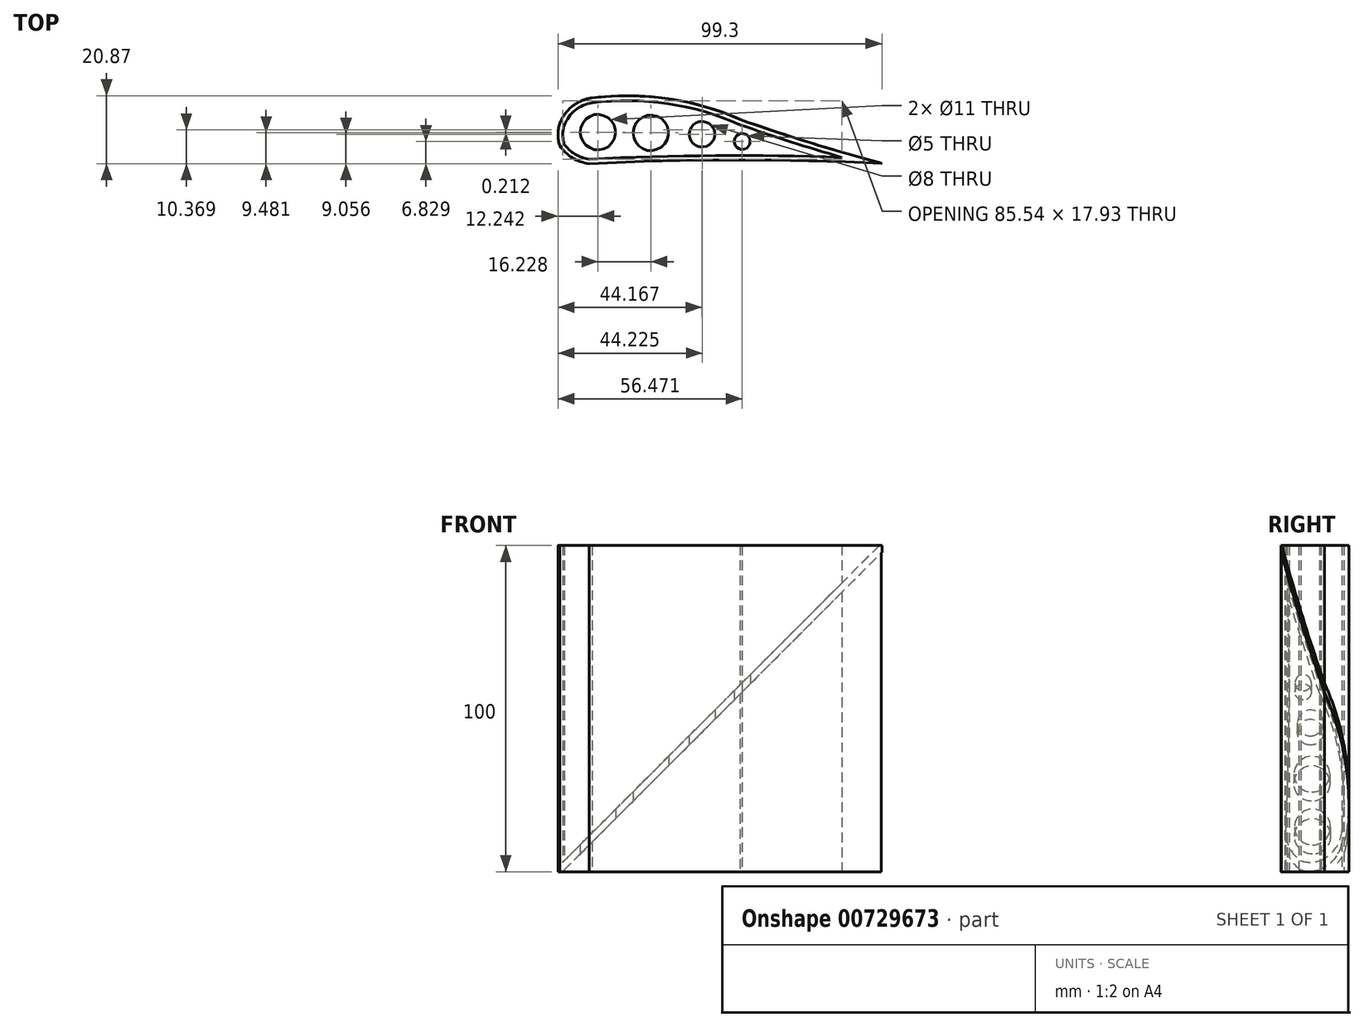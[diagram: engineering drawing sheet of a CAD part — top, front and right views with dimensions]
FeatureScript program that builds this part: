
annotation { "Feature Type Name" : "Feature", "Feature Type Description" : "" }
export const myFeature = defineFeature(function(context is Context, id is Id, definition is map)
    precondition{}
    {
        {
            var Q0;
            Q0=qCreatedBy(makeId("Top.planeOp"),FACE);
            var sketch = newSketch(context, id + "F0", { "sketchPlane" : qUnion([Q0])});
            skArc(sketch, "E0", {"start": v(-50.4, 5.52) * mm, "mid": v(-46.5, 1.8) * mm, "end": v(-41.43, 0) * mm});
            skArc(sketch, "E1", {"start": v(-50.4, 12.4) * mm, "mid": v(-50.96, 8.96) * mm, "end": v(-50.4, 5.52) * mm});
            skArc(sketch, "E2", {"start": v(-40.6, 20.25) * mm, "mid": v(-46.58, 17.68) * mm, "end": v(-50.4, 12.4) * mm});
            skArc(sketch, "E3", {"start": v(5.5, 13.44) * mm, "mid": v(-17.09, 20.01) * mm, "end": v(-40.6, 20.25) * mm});
            skArc(sketch, "E4", {"start": v(5.5, 13.44) * mm, "mid": v(27.14, 6.3) * mm, "end": v(49.04, 0) * mm});
            skArc(sketch, "E5", {"start": v(49.04, 0) * mm, "mid": v(3.8, 1.13) * mm, "end": v(-41.43, 0) * mm});
            skLineSegment(sketch, "E6", {"start": v(-50.96, 18.95) * mm, "end": v(-50.96, 0) * mm});
            skLineSegment(sketch, "E7", {"start": v(49.04, 0) * mm, "end": v(49.04, 12.24) * mm});
            skArc(sketch, "E8.0", {"start": v(4.93, 12.05) * mm, "mid": v(-17.27, 18.52) * mm, "end": v(-40.4, 18.76) * mm});
            skArc(sketch, "E8.1", {"start": v(-48.98, 11.9) * mm, "mid": v(-49.45, 9.05) * mm, "end": v(-49.04, 6.2) * mm});
            skArc(sketch, "E8.2", {"start": v(-49.04, 6.2) * mm, "mid": v(-45.68, 3.06) * mm, "end": v(-41.36, 1.5) * mm});
            skArc(sketch, "E8.3", {"start": v(-40.4, 18.76) * mm, "mid": v(-45.63, 16.51) * mm, "end": v(-48.98, 11.9) * mm});
            skArc(sketch, "E8.4", {"start": v(36.09, 2.06) * mm, "mid": v(-2.65, 2.6) * mm, "end": v(-41.36, 1.5) * mm});
            skArc(sketch, "E8.5", {"start": v(4.93, 12.05) * mm, "mid": v(20.44, 6.84) * mm, "end": v(36.09, 2.06) * mm});
            skSolve(sketch);
        }
        {
            var Q0;
            Q0=qCreatedBy(makeId("Front.planeOp"),FACE);
            var sketch = newSketch(context, id + "F1", { "sketchPlane" : qUnion([Q0])});
            skLineSegment(sketch, "E9", {"start": v(-50.95, 0) * mm, "end": v(-50.95, 1.41) * mm});
            skLineSegment(sketch, "E10", {"start": v(-50.95, 0) * mm, "end": v(-49.53, 0) * mm});
            skLineSegment(sketch, "E11.MirrorCS", {"start": v(49.05, 100) * mm, "end": v(47.64, 100) * mm});
            skLineSegment(sketch, "E12.MirrorCS", {"start": v(49.05, 100) * mm, "end": v(49.05, 98.59) * mm});
            skLineSegment(sketch, "E13", {"start": v(-50.95, 1.41) * mm, "end": v(47.64, 100) * mm});
            skLineSegment(sketch, "E14", {"start": v(49.05, 98.59) * mm, "end": v(-49.53, 0) * mm});
            skSolve(sketch);
        }
        {
            var Q0;
            Q0=qCreatedBy(makeId("Top.planeOp"),FACE);
            var sketch = newSketch(context, id + "F2", { "sketchPlane" : qUnion([Q0])});
            skArc(sketch, "E15", {"start": v(-50.35, 5.62) * mm, "mid": v(-46.46, 1.91) * mm, "end": v(-41.4, 0.1) * mm});
            skArc(sketch, "E16", {"start": v(-50.35, 12.44) * mm, "mid": v(-50.9, 9.03) * mm, "end": v(-50.35, 5.62) * mm});
            skArc(sketch, "E17", {"start": v(-40.56, 20.28) * mm, "mid": v(-46.54, 17.71) * mm, "end": v(-50.35, 12.44) * mm});
            skArc(sketch, "E18", {"start": v(5.48, 13.48) * mm, "mid": v(-17.07, 20.05) * mm, "end": v(-40.56, 20.28) * mm});
            skArc(sketch, "E19", {"start": v(5.48, 13.48) * mm, "mid": v(26.81, 6.44) * mm, "end": v(48.4, 0.21) * mm});
            skArc(sketch, "E20", {"start": v(48.4, 0.21) * mm, "mid": v(3.5, 1.27) * mm, "end": v(-41.4, 0.1) * mm});
            skLineSegment(sketch, "E21.bottom", {"start": v(-65.42, 35.82) * mm, "end": v(65.5, 35.82) * mm});
            skLineSegment(sketch, "E21.top", {"start": v(-65.42, -21.35) * mm, "end": v(65.5, -21.35) * mm});
            skLineSegment(sketch, "E21.left", {"start": v(-65.42, 35.82) * mm, "end": v(-65.42, -21.35) * mm});
            skLineSegment(sketch, "E21.right", {"start": v(65.5, 35.82) * mm, "end": v(65.5, -21.35) * mm});
            skSolve(sketch);
        }
        {
            var Q0;
            {var subQ0=sQuery(id+"F0.wireOp",EDGE,"E0");Q0=makeQuery(id+"F0.imprint","IMPRINT",FACE,{"disambiguationData":[TD([[makeQuery(id+"F0.imprint","IMPRINT",EDGE,{"derivedFrom":subQ0}),1.0]])]});}
            extrude(context, id + "F3", {"entities" : qUnion([Q0]), "depth" : 100 * mm, "offsetDistance" : 25 * mm});
        }
        {
            var Q0;
            Q0=makeQuery(id+"F1.imprint","IMPRINT",FACE,{"disambiguationData":[TD([[makeQuery(id+"F1.imprint","IMPRINT",EDGE,{"derivedFrom":sQuery(id+"F1.wireOp",EDGE,"E9")}),-1.0]])]});
            extrude(context, id + "F4", {"entities" : qUnion([Q0]), "operationType" : NewBodyOperationType.ADD, "oppositeDirection" : true, "depth" : 25 * mm, "offsetDistance" : 25 * mm});
        }
        {
            var Q0;
            Q0=makeQuery(id+"F2.imprint","IMPRINT",FACE,{"disambiguationData":[TD([[makeQuery(id+"F2.imprint","IMPRINT",EDGE,{"derivedFrom":sQuery(id+"F2.wireOp",EDGE,"E15")}),-1.0]])]});
            var Q1;
            Q1=makeQuery(id+"F3.opExtrude","CAP_FACE",FACE,{"disambiguationData":[OSD([sQuery(id+"F0.wireOp",EDGE,"E0"),sQuery(id+"F0.wireOp",EDGE,"E1"),sQuery(id+"F0.wireOp",EDGE,"E2"),sQuery(id+"F0.wireOp",EDGE,"E3"),sQuery(id+"F0.wireOp",EDGE,"E4"),sQuery(id+"F0.wireOp",EDGE,"E5"),sQuery(id+"F0.wireOp",EDGE,"E8.0"),sQuery(id+"F0.wireOp",EDGE,"E8.1"),sQuery(id+"F0.wireOp",EDGE,"E8.2"),sQuery(id+"F0.wireOp",EDGE,"E8.3"),sQuery(id+"F0.wireOp",EDGE,"E8.4"),sQuery(id+"F0.wireOp",EDGE,"E8.5")])],"isStart":false});
            var Q2;
            Q2=makeQuery(id+"F3.opExtrude","CAP_FACE",FACE,{"disambiguationData":[OSD([sQuery(id+"F0.wireOp",EDGE,"E0"),sQuery(id+"F0.wireOp",EDGE,"E1"),sQuery(id+"F0.wireOp",EDGE,"E2"),sQuery(id+"F0.wireOp",EDGE,"E3"),sQuery(id+"F0.wireOp",EDGE,"E4"),sQuery(id+"F0.wireOp",EDGE,"E5"),sQuery(id+"F0.wireOp",EDGE,"E8.0"),sQuery(id+"F0.wireOp",EDGE,"E8.1"),sQuery(id+"F0.wireOp",EDGE,"E8.2"),sQuery(id+"F0.wireOp",EDGE,"E8.3"),sQuery(id+"F0.wireOp",EDGE,"E8.4"),sQuery(id+"F0.wireOp",EDGE,"E8.5")])],"isStart":true});
            extrude(context, id + "F5", {"entities" : qUnion([Q0]), "operationType" : NewBodyOperationType.REMOVE, "depth" : 100 * mm, "endBoundEntityFace" : qUnion([Q1]), "offsetDistance" : 25 * mm});
        }
        {
            var Q0;
            Q0=qCreatedBy(makeId("Top.planeOp"),FACE);
            var sketch = newSketch(context, id + "F6", { "sketchPlane" : qUnion([Q0])});
            skCircle(sketch, "E22", {"center": v(-38.67, 9.8) * mm, "radius": 5.5 * mm});
            skCircle(sketch, "E23", {"center": v(-22.44, 9.58) * mm, "radius": 5.5 * mm});
            skCircle(sketch, "E24", {"center": v(-6.74, 9.16) * mm, "radius": 4 * mm});
            skCircle(sketch, "E25", {"center": v(5.56, 6.93) * mm, "radius": 2.5 * mm});
            skSolve(sketch);
        }
        {
            var Q0;
            Q0 = qSketchRegion(id + "F6", true);
            extrude(context, id + "F7", {"entities" : qUnion([Q0]), "operationType" : NewBodyOperationType.REMOVE, "depth" : 100 * mm, "offsetDistance" : 25 * mm});
        }
    });
